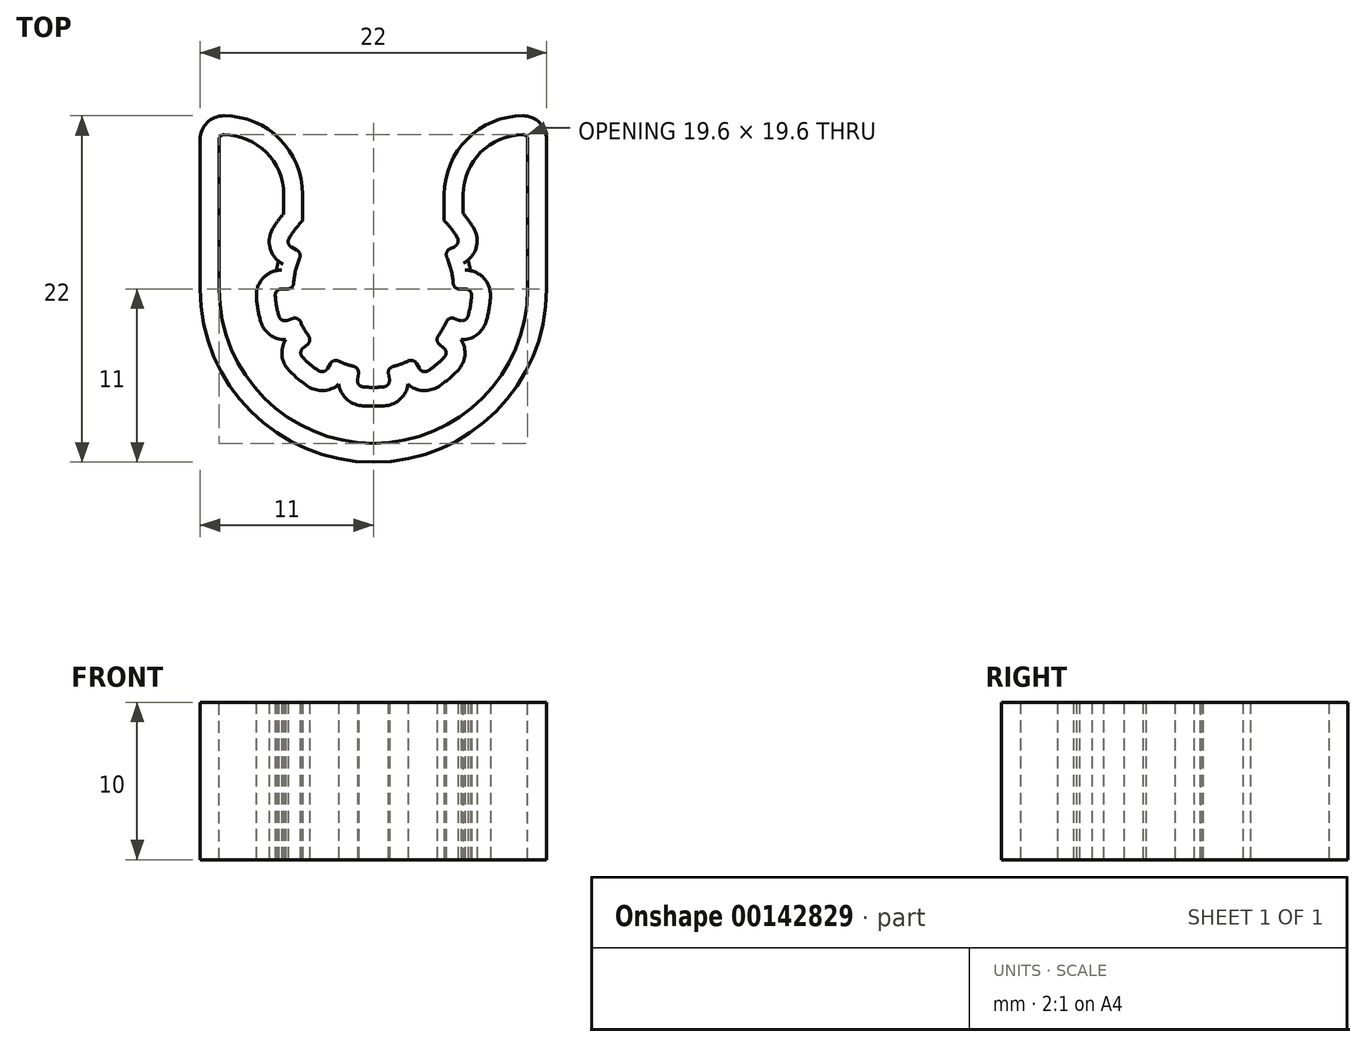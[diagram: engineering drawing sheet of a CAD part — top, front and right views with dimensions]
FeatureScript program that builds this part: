
annotation { "Feature Type Name" : "Feature", "Feature Type Description" : "" }
export const myFeature = defineFeature(function(context is Context, id is Id, definition is map)
    precondition{}
    {
        {
            var Q0;
            Q0=qCreatedBy(makeId("Top.planeOp"),FACE);
            var sketch = newSketch(context, id + "F0", { "sketchPlane" : qUnion([Q0])});
            skArc(sketch, "E0", {"start": v(-4.68, 1.97) * mm, "mid": v(-4.94, 1.19) * mm, "end": v(-5.07, 0.37) * mm});
            skArc(sketch, "E1", {"start": v(-11, 0) * mm, "mid": v(0, -11) * mm, "end": v(11, 0) * mm});
            skLineSegment(sketch, "E2.left", {"start": v(-11, 0) * mm, "end": v(-11, 9.5) * mm});
            skLineSegment(sketch, "E2.right", {"start": v(11, 0) * mm, "end": v(11, 9.5) * mm});
            skLineSegment(sketch, "E3", {"start": v(-9.5, 11) * mm, "end": v(-9.5, 11) * mm});
            skLineSegment(sketch, "E4", {"start": v(-4.5, 4.34) * mm, "end": v(-4.5, 6) * mm});
            skLineSegment(sketch, "E5", {"start": v(4.5, 4.34) * mm, "end": v(4.5, 6) * mm});
            skLineSegment(sketch, "E6.trimOffspring", {"start": v(9.5, 11) * mm, "end": v(9.5, 11) * mm});
            skPoint(sketch, "E7.orphan", {"position": v(-4.5, 19.15) * mm});
            skPoint(sketch, "E8.orphan", {"position": v(4.5, 18.53) * mm});
            skPoint(sketch, "E9.third.point", {"position": v(-104.28, 11) * mm});
            skPoint(sketch, "E10.third.point", {"position": v(64.61, 54.62) * mm});
            skPoint(sketch, "E11.orphan", {"position": v(4.5, 0) * mm});
            skPoint(sketch, "E12.orphan", {"position": v(-4.5, 0) * mm});
            skArc(sketch, "E13", {"start": v(-6.24, -0.43) * mm, "mid": v(-6.16, -1.09) * mm, "end": v(-6, -1.73) * mm});
            skLineSegment(sketch, "E14", {"start": v(-5.47, 0) * mm, "end": v(-5.84, 0) * mm});
            skLineSegment(sketch, "E15", {"start": v(5.47, 0) * mm, "end": v(5.84, 0) * mm});
            skLineSegment(sketch, "E16", {"start": v(-5.14, -1.87) * mm, "end": v(-5.48, -2) * mm});
            skArc(sketch, "E17.trimOffspring", {"start": v(-4.63, -2.08) * mm, "mid": v(-4.4, -2.54) * mm, "end": v(-4.12, -2.97) * mm});
            skLineSegment(sketch, "E18", {"start": v(-4.19, -3.51) * mm, "end": v(-4.47, -3.75) * mm});
            skLineSegment(sketch, "E19", {"start": v(-2.73, -4.73) * mm, "end": v(-2.92, -5.05) * mm});
            skLineSegment(sketch, "E20", {"start": v(-0.95, -5.38) * mm, "end": v(-1.01, -5.75) * mm});
            skArc(sketch, "E21.trimOffspring", {"start": v(-2.21, -4.57) * mm, "mid": v(-1.74, -4.77) * mm, "end": v(-1.24, -4.93) * mm});
            skLineSegment(sketch, "E22", {"start": v(0.95, -5.38) * mm, "end": v(1.01, -5.75) * mm});
            skArc(sketch, "E23.trimOffspring", {"start": v(1.24, -4.93) * mm, "mid": v(1.74, -4.77) * mm, "end": v(2.21, -4.57) * mm});
            skArc(sketch, "E24.trimOffspring", {"start": v(-0.66, -6.21) * mm, "mid": v(0, -6.25) * mm, "end": v(0.66, -6.21) * mm});
            skArc(sketch, "E25.trimOffspring", {"start": v(-4.5, -4.34) * mm, "mid": v(-4.02, -4.79) * mm, "end": v(-3.49, -5.19) * mm});
            skLineSegment(sketch, "E26", {"start": v(2.73, -4.73) * mm, "end": v(2.92, -5.05) * mm});
            skArc(sketch, "E27.trimOffspring", {"start": v(3.49, -5.19) * mm, "mid": v(4.02, -4.79) * mm, "end": v(4.5, -4.34) * mm});
            skLineSegment(sketch, "E28", {"start": v(4.19, -3.51) * mm, "end": v(4.47, -3.75) * mm});
            skLineSegment(sketch, "E29", {"start": v(5.14, -1.87) * mm, "end": v(5.48, -2) * mm});
            skArc(sketch, "E30.trimOffspring", {"start": v(4.12, -2.97) * mm, "mid": v(4.4, -2.54) * mm, "end": v(4.63, -2.08) * mm});
            skArc(sketch, "E31.trimOffspring", {"start": v(5.07, 0.37) * mm, "mid": v(4.93, 1.21) * mm, "end": v(4.66, 2.02) * mm});
            skArc(sketch, "E32.trimOffspring", {"start": v(6, -1.73) * mm, "mid": v(6.16, -1.09) * mm, "end": v(6.24, -0.43) * mm});
            skLineSegment(sketch, "E33", {"start": v(4.84, 2.54) * mm, "end": v(5.17, 2.7) * mm});
            skLineSegment(sketch, "E34", {"start": v(-4.87, 2.48) * mm, "end": v(-5.2, 2.65) * mm});
            skArc(sketch, "E35.trimOffspring", {"start": v(-4.5, 4.34) * mm, "mid": v(-4.96, 3.8) * mm, "end": v(-5.36, 3.21) * mm});
            skPoint(sketch, "E36.visualSharp", {"position": v(4.5, 11) * mm});
            skArc(sketch, "E36.filletArc", {"start": v(9.5, 11) * mm, "mid": v(5.96, 9.54) * mm, "end": v(4.5, 6) * mm});
            skPoint(sketch, "E37.visualSharp", {"position": v(-4.5, 11) * mm});
            skArc(sketch, "E37.filletArc", {"start": v(-4.5, 6) * mm, "mid": v(-5.96, 9.54) * mm, "end": v(-9.5, 11) * mm});
            skPoint(sketch, "E38.visualSharp", {"position": v(11, 11) * mm});
            skArc(sketch, "E38.filletArc", {"start": v(11, 9.5) * mm, "mid": v(10.56, 10.56) * mm, "end": v(9.5, 11) * mm});
            skPoint(sketch, "E39.visualSharp", {"position": v(-11, 11) * mm});
            skArc(sketch, "E39.filletArc", {"start": v(-9.5, 11) * mm, "mid": v(-10.56, 10.56) * mm, "end": v(-11, 9.5) * mm});
            skArc(sketch, "E40.trimOffspring", {"start": v(5.33, 3.27) * mm, "mid": v(4.94, 3.83) * mm, "end": v(4.5, 4.34) * mm});
            skPoint(sketch, "E41.visualSharp", {"position": v(-5.57, 2.84) * mm});
            skArc(sketch, "E41.filletArc", {"start": v(-5.36, 3.21) * mm, "mid": v(-5.4, 2.9) * mm, "end": v(-5.2, 2.65) * mm});
            skPoint(sketch, "E42.visualSharp", {"position": v(5.54, 2.9) * mm});
            skArc(sketch, "E42.filletArc", {"start": v(5.17, 2.7) * mm, "mid": v(5.37, 2.96) * mm, "end": v(5.33, 3.27) * mm});
            skPoint(sketch, "E43.visualSharp", {"position": v(6.25, 0) * mm});
            skArc(sketch, "E43.filletArc", {"start": v(6.24, -0.43) * mm, "mid": v(6.13, -0.13) * mm, "end": v(5.84, 0) * mm});
            skPoint(sketch, "E44.visualSharp", {"position": v(5.87, -2.14) * mm});
            skArc(sketch, "E44.filletArc", {"start": v(5.48, -2) * mm, "mid": v(5.8, -1.98) * mm, "end": v(6, -1.73) * mm});
            skPoint(sketch, "E45.visualSharp", {"position": v(4.79, -4.02) * mm});
            skArc(sketch, "E45.filletArc", {"start": v(4.5, -4.34) * mm, "mid": v(4.61, -4.04) * mm, "end": v(4.47, -3.75) * mm});
            skPoint(sketch, "E46.visualSharp", {"position": v(3.12, -5.41) * mm});
            skArc(sketch, "E46.filletArc", {"start": v(2.92, -5.05) * mm, "mid": v(3.17, -5.24) * mm, "end": v(3.49, -5.19) * mm});
            skPoint(sketch, "E47.visualSharp", {"position": v(1.09, -6.16) * mm});
            skArc(sketch, "E47.filletArc", {"start": v(0.66, -6.21) * mm, "mid": v(0.94, -6.06) * mm, "end": v(1.01, -5.75) * mm});
            skPoint(sketch, "E48.visualSharp", {"position": v(-1.09, -6.16) * mm});
            skArc(sketch, "E48.filletArc", {"start": v(-1.01, -5.75) * mm, "mid": v(-0.94, -6.06) * mm, "end": v(-0.66, -6.21) * mm});
            skPoint(sketch, "E49.visualSharp", {"position": v(-3.12, -5.41) * mm});
            skArc(sketch, "E49.filletArc", {"start": v(-3.49, -5.19) * mm, "mid": v(-3.17, -5.24) * mm, "end": v(-2.92, -5.05) * mm});
            skPoint(sketch, "E50.visualSharp", {"position": v(-4.79, -4.02) * mm});
            skArc(sketch, "E50.filletArc", {"start": v(-4.47, -3.75) * mm, "mid": v(-4.61, -4.04) * mm, "end": v(-4.5, -4.34) * mm});
            skPoint(sketch, "E51.visualSharp", {"position": v(-5.87, -2.14) * mm});
            skArc(sketch, "E51.filletArc", {"start": v(-6, -1.73) * mm, "mid": v(-5.8, -1.98) * mm, "end": v(-5.48, -2) * mm});
            skPoint(sketch, "E52.visualSharp", {"position": v(-6.25, 0) * mm});
            skArc(sketch, "E52.filletArc", {"start": v(-5.84, 0) * mm, "mid": v(-6.13, -0.13) * mm, "end": v(-6.24, -0.43) * mm});
            skPoint(sketch, "E53.visualSharp", {"position": v(-4.77, -1.74) * mm});
            skArc(sketch, "E53.filletArc", {"start": v(-4.63, -2.08) * mm, "mid": v(-4.84, -1.88) * mm, "end": v(-5.14, -1.87) * mm});
            skPoint(sketch, "E54.visualSharp", {"position": v(-3.9, -3.27) * mm});
            skArc(sketch, "E54.filletArc", {"start": v(-4.19, -3.51) * mm, "mid": v(-4.05, -3.26) * mm, "end": v(-4.12, -2.97) * mm});
            skPoint(sketch, "E55.visualSharp", {"position": v(-2.54, -4.4) * mm});
            skArc(sketch, "E55.filletArc", {"start": v(-2.21, -4.57) * mm, "mid": v(-2.5, -4.55) * mm, "end": v(-2.73, -4.73) * mm});
            skPoint(sketch, "E56.visualSharp", {"position": v(-0.88, -5) * mm});
            skArc(sketch, "E56.filletArc", {"start": v(-0.95, -5.38) * mm, "mid": v(-1, -5.1) * mm, "end": v(-1.24, -4.93) * mm});
            skPoint(sketch, "E57.visualSharp", {"position": v(0.88, -5) * mm});
            skArc(sketch, "E57.filletArc", {"start": v(1.24, -4.93) * mm, "mid": v(1, -5.1) * mm, "end": v(0.95, -5.38) * mm});
            skPoint(sketch, "E58.visualSharp", {"position": v(2.54, -4.4) * mm});
            skArc(sketch, "E58.filletArc", {"start": v(2.73, -4.73) * mm, "mid": v(2.5, -4.55) * mm, "end": v(2.21, -4.57) * mm});
            skPoint(sketch, "E59.visualSharp", {"position": v(3.9, -3.27) * mm});
            skArc(sketch, "E59.filletArc", {"start": v(4.12, -2.97) * mm, "mid": v(4.05, -3.26) * mm, "end": v(4.19, -3.51) * mm});
            skPoint(sketch, "E60.visualSharp", {"position": v(5.08, 0) * mm});
            skArc(sketch, "E60.filletArc", {"start": v(5.07, 0.37) * mm, "mid": v(5.2, 0.1) * mm, "end": v(5.47, 0) * mm});
            skPoint(sketch, "E61.visualSharp", {"position": v(4.77, -1.74) * mm});
            skArc(sketch, "E61.filletArc", {"start": v(5.14, -1.87) * mm, "mid": v(4.84, -1.88) * mm, "end": v(4.63, -2.08) * mm});
            skPoint(sketch, "E62.visualSharp", {"position": v(4.5, 2.36) * mm});
            skArc(sketch, "E62.filletArc", {"start": v(4.84, 2.54) * mm, "mid": v(4.65, 2.31) * mm, "end": v(4.66, 2.02) * mm});
            skPoint(sketch, "E63.visualSharp", {"position": v(-5.08, 0) * mm});
            skArc(sketch, "E63.filletArc", {"start": v(-5.47, 0) * mm, "mid": v(-5.2, 0.1) * mm, "end": v(-5.07, 0.37) * mm});
            skArc(sketch, "E64.filletArc", {"start": v(-4.68, 1.97) * mm, "mid": v(-4.67, 2.26) * mm, "end": v(-4.87, 2.48) * mm});
            skSolve(sketch);
        }
        {
            var Q0;
            Q0 = qSketchRegion(id + "F0", true);
            extrude(context, id + "F1", {"entities" : qUnion([Q0]), "depth" : 10 * mm, "offsetDistance" : 25 * mm});
        }
        {
            var Q0;
            Q0=makeQuery(id+"F1.opExtrude","CAP_FACE",FACE,{"disambiguationData":[OSD([sQuery(id+"F0.wireOp",EDGE,"E0"),sQuery(id+"F0.wireOp",EDGE,"E1"),sQuery(id+"F0.wireOp",EDGE,"E2.left"),sQuery(id+"F0.wireOp",EDGE,"E2.right"),sQuery(id+"F0.wireOp",EDGE,"E4"),sQuery(id+"F0.wireOp",EDGE,"E5"),sQuery(id+"F0.wireOp",EDGE,"E13"),sQuery(id+"F0.wireOp",EDGE,"E14"),sQuery(id+"F0.wireOp",EDGE,"E15"),sQuery(id+"F0.wireOp",EDGE,"E16"),sQuery(id+"F0.wireOp",EDGE,"E17.trimOffspring"),sQuery(id+"F0.wireOp",EDGE,"E18"),sQuery(id+"F0.wireOp",EDGE,"E19"),sQuery(id+"F0.wireOp",EDGE,"E20"),sQuery(id+"F0.wireOp",EDGE,"E21.trimOffspring"),sQuery(id+"F0.wireOp",EDGE,"E22"),sQuery(id+"F0.wireOp",EDGE,"E23.trimOffspring"),sQuery(id+"F0.wireOp",EDGE,"E24.trimOffspring"),sQuery(id+"F0.wireOp",EDGE,"E25.trimOffspring"),sQuery(id+"F0.wireOp",EDGE,"E26"),sQuery(id+"F0.wireOp",EDGE,"E27.trimOffspring"),sQuery(id+"F0.wireOp",EDGE,"E28"),sQuery(id+"F0.wireOp",EDGE,"E29"),sQuery(id+"F0.wireOp",EDGE,"E30.trimOffspring"),sQuery(id+"F0.wireOp",EDGE,"E31.trimOffspring"),sQuery(id+"F0.wireOp",EDGE,"E32.trimOffspring"),sQuery(id+"F0.wireOp",EDGE,"E33"),sQuery(id+"F0.wireOp",EDGE,"E34"),sQuery(id+"F0.wireOp",EDGE,"E35.trimOffspring"),sQuery(id+"F0.wireOp",EDGE,"E36.filletArc"),sQuery(id+"F0.wireOp",EDGE,"E37.filletArc"),sQuery(id+"F0.wireOp",EDGE,"E38.filletArc"),sQuery(id+"F0.wireOp",EDGE,"E39.filletArc"),sQuery(id+"F0.wireOp",EDGE,"E40.trimOffspring"),sQuery(id+"F0.wireOp",EDGE,"E41.filletArc"),sQuery(id+"F0.wireOp",EDGE,"E42.filletArc"),sQuery(id+"F0.wireOp",EDGE,"E43.filletArc"),sQuery(id+"F0.wireOp",EDGE,"E44.filletArc"),sQuery(id+"F0.wireOp",EDGE,"E45.filletArc"),sQuery(id+"F0.wireOp",EDGE,"E46.filletArc"),sQuery(id+"F0.wireOp",EDGE,"E47.filletArc"),sQuery(id+"F0.wireOp",EDGE,"E48.filletArc"),sQuery(id+"F0.wireOp",EDGE,"E49.filletArc"),sQuery(id+"F0.wireOp",EDGE,"E50.filletArc"),sQuery(id+"F0.wireOp",EDGE,"E51.filletArc"),sQuery(id+"F0.wireOp",EDGE,"E52.filletArc"),sQuery(id+"F0.wireOp",EDGE,"E53.filletArc"),sQuery(id+"F0.wireOp",EDGE,"E54.filletArc"),sQuery(id+"F0.wireOp",EDGE,"E55.filletArc"),sQuery(id+"F0.wireOp",EDGE,"E56.filletArc"),sQuery(id+"F0.wireOp",EDGE,"E57.filletArc"),sQuery(id+"F0.wireOp",EDGE,"E58.filletArc"),sQuery(id+"F0.wireOp",EDGE,"E59.filletArc"),sQuery(id+"F0.wireOp",EDGE,"E60.filletArc"),sQuery(id+"F0.wireOp",EDGE,"E61.filletArc"),sQuery(id+"F0.wireOp",EDGE,"E62.filletArc"),sQuery(id+"F0.wireOp",EDGE,"E63.filletArc"),sQuery(id+"F0.wireOp",EDGE,"E64.filletArc")])],"isStart":false});
            var Q1;
            Q1=makeQuery(id+"F1.opExtrude","CAP_FACE",FACE,{"disambiguationData":[OSD([sQuery(id+"F0.wireOp",EDGE,"E0"),sQuery(id+"F0.wireOp",EDGE,"E1"),sQuery(id+"F0.wireOp",EDGE,"E2.left"),sQuery(id+"F0.wireOp",EDGE,"E2.right"),sQuery(id+"F0.wireOp",EDGE,"E4"),sQuery(id+"F0.wireOp",EDGE,"E5"),sQuery(id+"F0.wireOp",EDGE,"E13"),sQuery(id+"F0.wireOp",EDGE,"E14"),sQuery(id+"F0.wireOp",EDGE,"E15"),sQuery(id+"F0.wireOp",EDGE,"E16"),sQuery(id+"F0.wireOp",EDGE,"E17.trimOffspring"),sQuery(id+"F0.wireOp",EDGE,"E18"),sQuery(id+"F0.wireOp",EDGE,"E19"),sQuery(id+"F0.wireOp",EDGE,"E20"),sQuery(id+"F0.wireOp",EDGE,"E21.trimOffspring"),sQuery(id+"F0.wireOp",EDGE,"E22"),sQuery(id+"F0.wireOp",EDGE,"E23.trimOffspring"),sQuery(id+"F0.wireOp",EDGE,"E24.trimOffspring"),sQuery(id+"F0.wireOp",EDGE,"E25.trimOffspring"),sQuery(id+"F0.wireOp",EDGE,"E26"),sQuery(id+"F0.wireOp",EDGE,"E27.trimOffspring"),sQuery(id+"F0.wireOp",EDGE,"E28"),sQuery(id+"F0.wireOp",EDGE,"E29"),sQuery(id+"F0.wireOp",EDGE,"E30.trimOffspring"),sQuery(id+"F0.wireOp",EDGE,"E31.trimOffspring"),sQuery(id+"F0.wireOp",EDGE,"E32.trimOffspring"),sQuery(id+"F0.wireOp",EDGE,"E33"),sQuery(id+"F0.wireOp",EDGE,"E34"),sQuery(id+"F0.wireOp",EDGE,"E35.trimOffspring"),sQuery(id+"F0.wireOp",EDGE,"E36.filletArc"),sQuery(id+"F0.wireOp",EDGE,"E37.filletArc"),sQuery(id+"F0.wireOp",EDGE,"E38.filletArc"),sQuery(id+"F0.wireOp",EDGE,"E39.filletArc"),sQuery(id+"F0.wireOp",EDGE,"E40.trimOffspring"),sQuery(id+"F0.wireOp",EDGE,"E41.filletArc"),sQuery(id+"F0.wireOp",EDGE,"E42.filletArc"),sQuery(id+"F0.wireOp",EDGE,"E43.filletArc"),sQuery(id+"F0.wireOp",EDGE,"E44.filletArc"),sQuery(id+"F0.wireOp",EDGE,"E45.filletArc"),sQuery(id+"F0.wireOp",EDGE,"E46.filletArc"),sQuery(id+"F0.wireOp",EDGE,"E47.filletArc"),sQuery(id+"F0.wireOp",EDGE,"E48.filletArc"),sQuery(id+"F0.wireOp",EDGE,"E49.filletArc"),sQuery(id+"F0.wireOp",EDGE,"E50.filletArc"),sQuery(id+"F0.wireOp",EDGE,"E51.filletArc"),sQuery(id+"F0.wireOp",EDGE,"E52.filletArc"),sQuery(id+"F0.wireOp",EDGE,"E53.filletArc"),sQuery(id+"F0.wireOp",EDGE,"E54.filletArc"),sQuery(id+"F0.wireOp",EDGE,"E55.filletArc"),sQuery(id+"F0.wireOp",EDGE,"E56.filletArc"),sQuery(id+"F0.wireOp",EDGE,"E57.filletArc"),sQuery(id+"F0.wireOp",EDGE,"E58.filletArc"),sQuery(id+"F0.wireOp",EDGE,"E59.filletArc"),sQuery(id+"F0.wireOp",EDGE,"E60.filletArc"),sQuery(id+"F0.wireOp",EDGE,"E61.filletArc"),sQuery(id+"F0.wireOp",EDGE,"E62.filletArc"),sQuery(id+"F0.wireOp",EDGE,"E63.filletArc"),sQuery(id+"F0.wireOp",EDGE,"E64.filletArc")])],"isStart":true});
            shell(context, id + "F2", {"entities" : qUnion([Q0, Q1]), "thickness" : 1.2 * mm});
        }
    });
